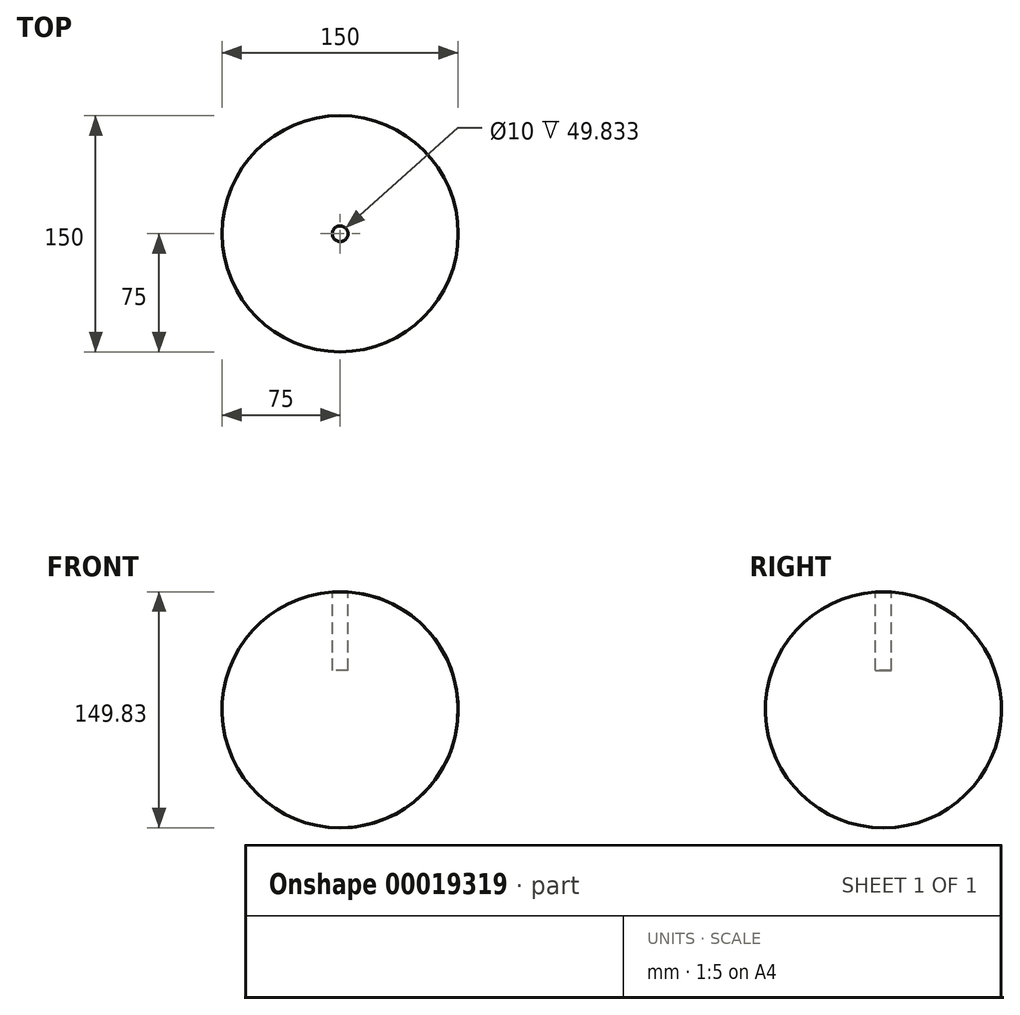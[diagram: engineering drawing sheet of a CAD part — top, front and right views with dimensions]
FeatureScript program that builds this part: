
annotation { "Feature Type Name" : "Feature", "Feature Type Description" : "" }
export const myFeature = defineFeature(function(context is Context, id is Id, definition is map)
    precondition{}
    {
        {
            var Q0;
            Q0=qCreatedBy(makeId("Front.planeOp"),FACE);
            var sketch = newSketch(context, id + "F0", { "sketchPlane" : qUnion([Q0])});
            skCircle(sketch, "E0", {"center": v(0, 0) * mm, "radius": 75 * mm});
            skLineSegment(sketch, "E1", {"start": v(0, 75) * mm, "end": v(0, -75) * mm});
            skSolve(sketch);
        }
        {
            var Q0;
            {var subQ0=sQuery(id+"F0.wireOp",EDGE,"E1");Q0=makeQuery(id+"F0.imprint","IMPRINT",FACE,{"disambiguationData":[TD([[makeQuery(id+"F0.imprint","IMPRINT",EDGE,{"derivedFrom":subQ0}),-1.0]])]});}
            var Q1;
            Q1=sQuery(id+"F0.wireOp",EDGE,"E0");
            var Q2;
            Q2=sQuery(id+"F0.wireOp",EDGE,"E1");
            revolve(context, id + "F1", {"entities" : qUnion([Q0]), "surfaceEntities" : qUnion([Q1]), "axis" : qUnion([Q2]), "revolveType" : RevolveType.FULL});
        }
        {
            var Q0;
            Q0=qCreatedBy(makeId("Top.planeOp"),FACE);
            cPlane(context, id + "F2", {"entities" : qUnion([Q0]), "cplaneType" : CPlaneType.OFFSET, "offset" : (150 / 2) * mm, "width" : 150 * mm, "height" : 150 * mm});
        }
        {
            var Q0;
            Q0=qCreatedBy(id+"F2.planeOp",FACE);
            var sketch = newSketch(context, id + "F3", { "sketchPlane" : qUnion([Q0])});
            skCircle(sketch, "E2", {"center": v(0, 0) * mm, "radius": 5 * mm});
            skSolve(sketch);
        }
        {
            var Q0;
            Q0=qSketchRegion(id+"F3",true);
            extrude(context, id + "F4", {"entities" : qUnion([Q0]), "operationType" : NewBodyOperationType.REMOVE, "oppositeDirection" : true, "depth" : 50 * mm});
        }
    });
